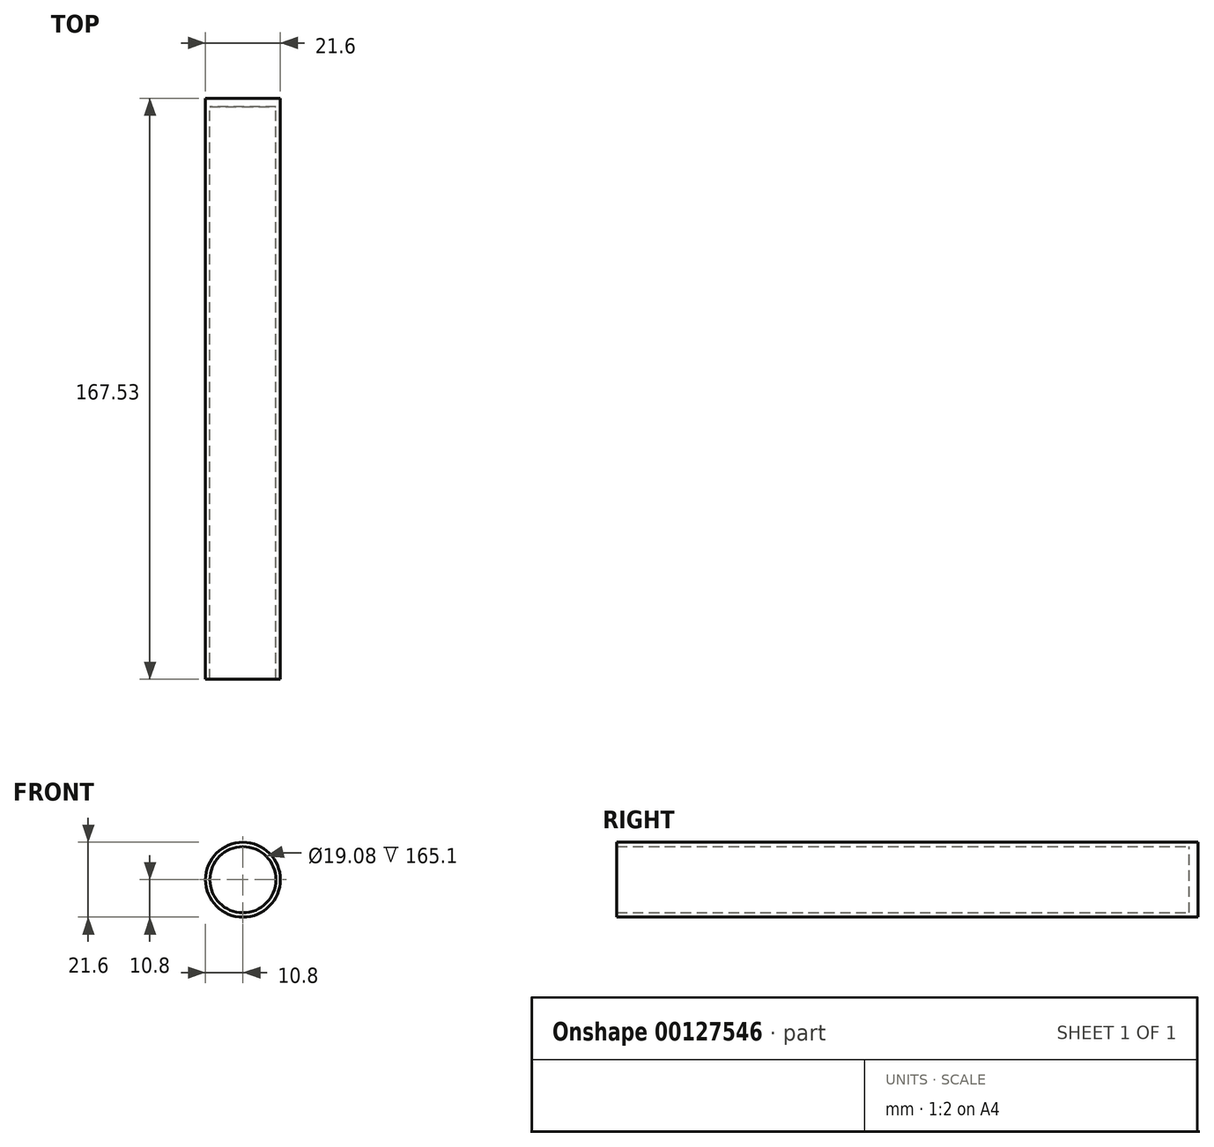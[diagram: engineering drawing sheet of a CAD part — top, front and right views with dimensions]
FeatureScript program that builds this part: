
annotation { "Feature Type Name" : "Feature", "Feature Type Description" : "" }
export const myFeature = defineFeature(function(context is Context, id is Id, definition is map)
    precondition{}
    {
        {
            var Q0;
            Q0=qCreatedBy(makeId("Front.planeOp"),FACE);
            var sketch = newSketch(context, id + "F0", { "sketchPlane" : qUnion([Q0])});
            skCircle(sketch, "E0", {"center": v(0, 0) * mm, "radius": 10.8 * mm});
            skCircle(sketch, "E1", {"center": v(0, 0) * mm, "radius": 9.54 * mm});
            skSolve(sketch);
        }
        {
            var Q0;
            Q0=qSketchRegion(id+"F0",true);
            var Q1;
            Q1=qSketchRegion(id+"FpAzvAZAPvuLyem_1",true);
            extrude(context, id + "F1", {"entities" : qUnion([Q0, Q1]), "depth" : 165.1 * mm});
        }
        {
            var Q0;
            Q0=qCreatedBy(makeId("Front.planeOp"),FACE);
            var sketch = newSketch(context, id + "F2", { "sketchPlane" : qUnion([Q0])});
            skCircle(sketch, "E2", {"center": v(0, 0) * mm, "radius": 10.8 * mm});
            skSolve(sketch);
        }
        {
            var Q0;
            Q0=makeQuery(id+"F2.imprint","IMPRINT",FACE,{"disambiguationData":[TD([[makeQuery(id+"F2.imprint","IMPRINT",EDGE,{"derivedFrom":sQuery(id+"F2.wireOp",EDGE,"E2")}),1.0]])]});
            extrude(context, id + "F3", {"entities" : qUnion([Q0]), "operationType" : NewBodyOperationType.ADD, "oppositeDirection" : true, "depth" : 2.43 * mm});
        }
    });
